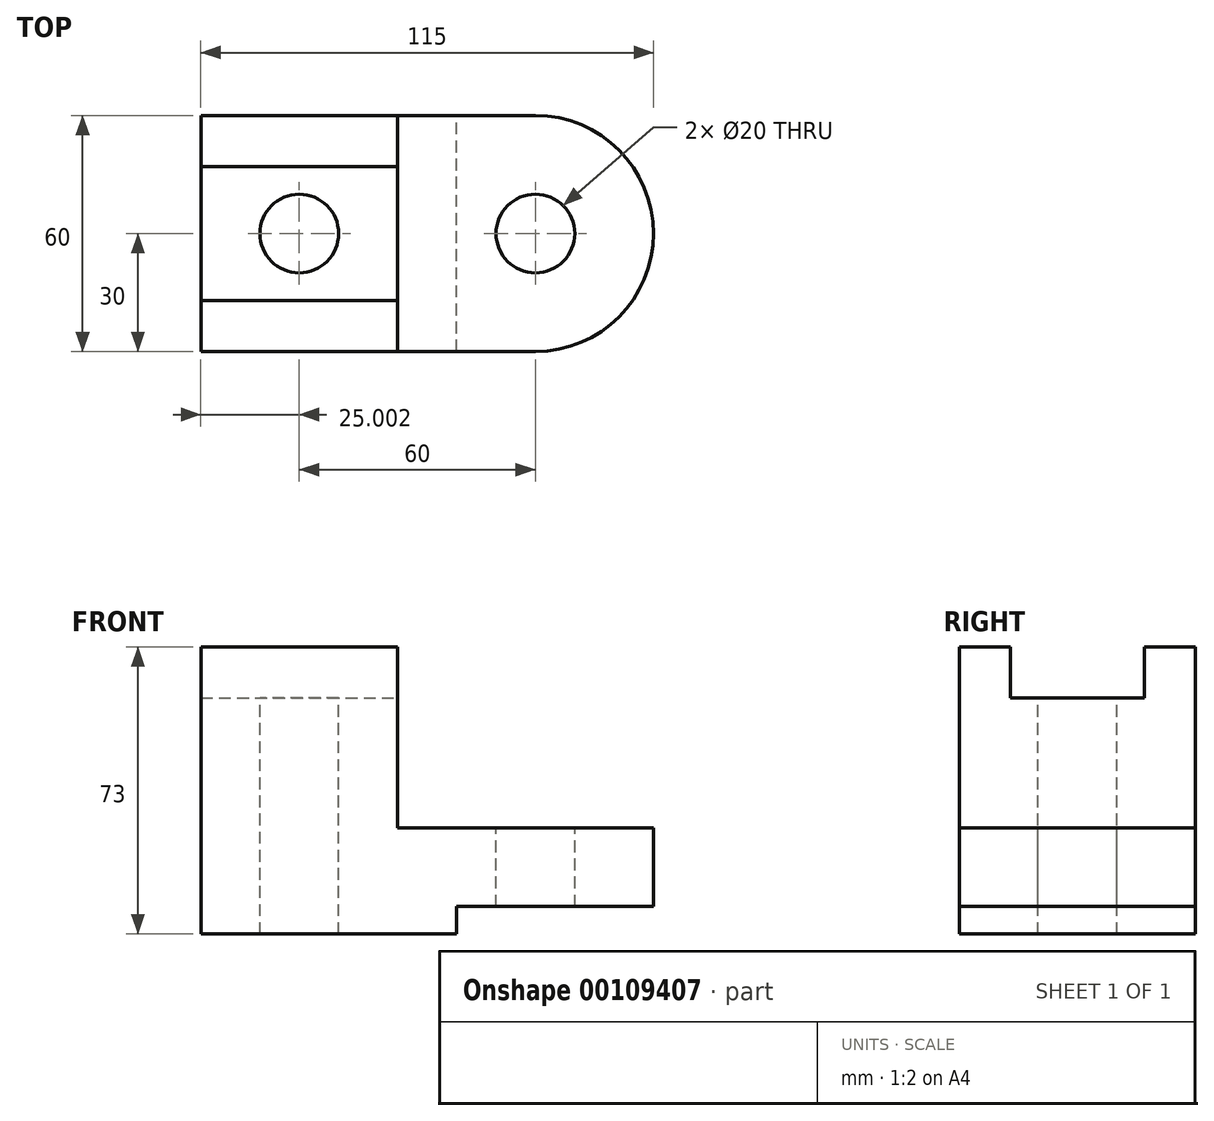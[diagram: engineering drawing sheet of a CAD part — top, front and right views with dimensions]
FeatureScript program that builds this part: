
annotation { "Feature Type Name" : "Feature", "Feature Type Description" : "" }
export const myFeature = defineFeature(function(context is Context, id is Id, definition is map)
    precondition{}
    {
        {
            var Q0;
            Q0=qCreatedBy(makeId("Front.planeOp"),FACE);
            var sketch = newSketch(context, id + "F0", { "sketchPlane" : qUnion([Q0])});
            skLineSegment(sketch, "E0", {"start": v(-44.24, 0) * mm, "end": v(-44.24, 60) * mm});
            skLineSegment(sketch, "E1", {"start": v(-44.24, 60) * mm, "end": v(5.76, 60) * mm});
            skLineSegment(sketch, "E2", {"start": v(5.76, 60) * mm, "end": v(5.76, 27) * mm});
            skPoint(sketch, "E3.start.orphan", {"position": v(14.75, 0) * mm});
            skLineSegment(sketch, "E4", {"start": v(5.76, 27) * mm, "end": v(70.76, 27) * mm});
            skLineSegment(sketch, "E5", {"start": v(70.76, 27) * mm, "end": v(70.76, 7) * mm});
            skLineSegment(sketch, "E6", {"start": v(70.76, 7) * mm, "end": v(20.76, 7) * mm});
            skLineSegment(sketch, "E7", {"start": v(20.76, 7) * mm, "end": v(20.76, 0) * mm});
            skLineSegment(sketch, "E8", {"start": v(20.76, 0) * mm, "end": v(-44.24, 0) * mm});
            skSolve(sketch);
        }
        {
            var Q0;
            Q0=makeQuery(id+"F0.imprint","IMPRINT",FACE,{"disambiguationData":[TD([[makeQuery(id+"F0.imprint","IMPRINT",EDGE,{"derivedFrom":sQuery(id+"F0.wireOp",EDGE,"E0")}),-1.0]])]});
            extrude(context, id + "F1", {"entities" : qUnion([Q0]), "depth" : 60 * mm});
        }
        {
            var Q0;
            Q0=makeQuery(id+"F1.opExtrude","SWEPT_FACE",FACE,{"disambiguationData":[OSD([sQuery(id+"F0.wireOp",EDGE,"E1")])]});
            var sketch = newSketch(context, id + "F2", { "sketchPlane" : qUnion([Q0])});
            skLineSegment(sketch, "E9", {"start": v(-44.24, 0) * mm, "end": v(-44.24, -13) * mm});
            skLineSegment(sketch, "E10", {"start": v(-44.24, -13) * mm, "end": v(5.76, -13) * mm});
            skLineSegment(sketch, "E11", {"start": v(5.76, -13) * mm, "end": v(5.76, 0) * mm});
            skLineSegment(sketch, "E12", {"start": v(-44.24, -60) * mm, "end": v(-44.24, -47) * mm});
            skLineSegment(sketch, "E13", {"start": v(-44.24, -47) * mm, "end": v(5.76, -47) * mm});
            skSolve(sketch);
        }
        {
            var Q0;
            Q0 = qSketchRegion(id + "F2", true);
            var Q1;
            Q1=makeQuery(id+"F2.imprint","IMPRINT",FACE,{"disambiguationData":[TD([[makeQuery(id+"F2.imprint","IMPRINT",EDGE,{"derivedFrom":sQuery(id+"F2.wireOp",EDGE,"E9")}),-1.0]])]});
            extrude(context, id + "F3", {"entities" : qUnion([Q0, Q1]), "operationType" : NewBodyOperationType.ADD, "depth" : 13 * mm});
        }
        {
            var Q0;
            Q0=makeQuery(id+"F1.opExtrude","SWEPT_FACE",FACE,{"disambiguationData":[OSD([sQuery(id+"F0.wireOp",EDGE,"E1")])]});
            var sketch = newSketch(context, id + "F4", { "sketchPlane" : qUnion([Q0])});
            skLineSegment(sketch, "E14", {"start": v(-44.24, -60) * mm, "end": v(-44.24, -47) * mm});
            skLineSegment(sketch, "E15", {"start": v(-44.24, -47) * mm, "end": v(5.76, -47) * mm});
            skLineSegment(sketch, "E16", {"start": v(5.76, -47) * mm, "end": v(5.76, -60) * mm});
            skSolve(sketch);
        }
        {
            var Q0;
            Q0 = qSketchRegion(id + "F4", true);
            var Q1;
            Q1=makeQuery(id+"F4.imprint","IMPRINT",FACE,{"disambiguationData":[TD([[makeQuery(id+"F4.imprint","IMPRINT",EDGE,{"derivedFrom":sQuery(id+"F4.wireOp",EDGE,"E14")}),-1.0]])]});
            extrude(context, id + "F5", {"entities" : qUnion([Q0, Q1]), "operationType" : NewBodyOperationType.ADD, "depth" : 13 * mm});
        }
        {
            var Q0;
            Q0=makeQuery(id+"F1.opExtrude","CAP_EDGE",EDGE,{"disambiguationData":[OSD([sQuery(id+"F0.wireOp",EDGE,"E5")])],"isStart":false});
            var Q1;
            Q1=makeQuery(id+"F1.opExtrude","CAP_EDGE",EDGE,{"disambiguationData":[OSD([sQuery(id+"F0.wireOp",EDGE,"E5")])],"isStart":true});
            fillet(context, id + "F6", {"entities" : qUnion([Q0, Q1]), "radius" : 30 * mm, "tangentPropagation" : true, "allowEdgeOverflow" : false});
        }
        {
            var Q0;
            Q0=makeQuery(id+"F1.opExtrude","SWEPT_FACE",FACE,{"disambiguationData":[OSD([sQuery(id+"F0.wireOp",EDGE,"E4")])]});
            var sketch = newSketch(context, id + "F7", { "sketchPlane" : qUnion([Q0])});
            skCircle(sketch, "E17", {"center": v(40.76, -30) * mm, "radius": 10 * mm});
            skSolve(sketch);
        }
        {
            var Q0;
            Q0=makeQuery(id+"F1.opExtrude","SWEPT_FACE",FACE,{"disambiguationData":[OSD([sQuery(id+"F0.wireOp",EDGE,"E1")])]});
            var sketch = newSketch(context, id + "F8", { "sketchPlane" : qUnion([Q0])});
            skCircle(sketch, "E18", {"center": v(-19.24, -30) * mm, "radius": 10 * mm});
            skPoint(sketch, "E19.orphan", {"position": v(-19.24, -13) * mm});
            skPoint(sketch, "E20.start.orphan", {"position": v(-19.24, -47) * mm});
            skSolve(sketch);
        }
        {
            var Q0;
            Q0=makeQuery(id+"F7.imprint","IMPRINT",FACE,{"disambiguationData":[TD([[makeQuery(id+"F7.imprint","IMPRINT",EDGE,{"derivedFrom":sQuery(id+"F7.wireOp",EDGE,"E17")}),1.0]])]});
            extrude(context, id + "F9", {"entities" : qUnion([Q0]), "operationType" : NewBodyOperationType.REMOVE, "oppositeDirection" : true, "depth" : 20 * mm});
        }
        {
            var Q0;
            Q0=makeQuery(id+"F8.imprint","IMPRINT",FACE,{"disambiguationData":[TD([[makeQuery(id+"F8.imprint","IMPRINT",EDGE,{"derivedFrom":sQuery(id+"F8.wireOp",EDGE,"E18")}),1.0]])]});
            extrude(context, id + "F10", {"entities" : qUnion([Q0]), "operationType" : NewBodyOperationType.REMOVE, "oppositeDirection" : true, "depth" : 60 * mm});
        }
    });
